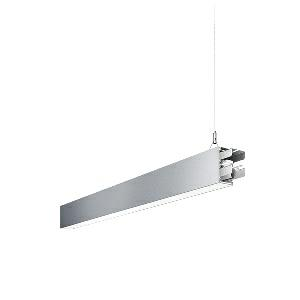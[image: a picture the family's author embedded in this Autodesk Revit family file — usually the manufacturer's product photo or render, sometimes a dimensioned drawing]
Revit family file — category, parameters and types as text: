
# Revit family: dotoo_line_-_dlp_1500_830_d_mid_00805845_2402
name_source: partatom
category: Lighting Fixtures
units: mm (PartAtom-declared; Revit-internal decimal feet)

## family parameters
Cut with Voids When Loaded = No
Host = Face
Light Source = No
Part Type = Normal
Room Calculation Point = No
Round Connector Dimension = Use Diameter
Shared = No

## types (1)
- DOTOO.line - DLP 1500/830/D MID (1 x LED, 1300 lm, 3000K)
    Apparent Load = 13 VA
    Approval mark = CE
    CIE Flux Codes = 67 91 98 100 100
    Color Rendering = 80-89
    Color Temperature = 3000K
    Control Gear = Electronic ballast
    Default Elevation = 1800 mm
    Description = DLP 1500/830/D|Suspended luminaire|light source: LED|connected load: 220-240 V, 50/60 Hz|Power consumption: approx. 13 W|standby: approx. 0,20|luminous flux: 1300 lm|luminous efficacy: 100 lm/W|light distribution: Direct|direct ratio: approx. 100 %|colour temperature: Warm white, ca. 3000 K|color rendering index (CRI): >= 80|chromaticity tolerance:  3 SDCM|System of protection: IP 40|technology: Continuously dimmable|luminaire body|material: Sectional aluminium|colour: Silver|lamp cover: Acrylic (PMMA), Clear|mains lead: 1,0 m With free stranded wires|Fastening: Steel cable 0.3 - 0.7 m|glare control: Prism aperture|luminance(L65): <= 3000 cd/m|unified glare rating(4H 8H): <=  19|special features: DALI Load 1x, TouchDIM - dimming via standard switch, Through-wired, up to 18 m on one mains connection, Flicker-free, Suitable as emergency lighting, Mechanical and electrical connection of the individual modules without tools|
    Frequency = 50 Hz
    Height = 110 mm
    Lamp = 1 x LED
    Lamp Light Flux = 1300 lm
    Lamp count = 1
    Length = 1122 mm
    Luminous efficacy = 100 lm/W
    Manufacturer = Waldmann
    ModVariant = No
    Model = 00805845
    Mounting Place = Ceiling
    Mounting Type = Pendant
    Number of Poles = 1
    OnlyDefault = Yes
    Power Factor = 1
    Product Name = DOTOO.line - DLP 1500/830/D MID
    Product group = Suspended luminaire
    ProductGroupID = 9
    Protection Class = Protection class I
    Protection Degree = IP 40
    RLX_Detail_Level = 1
    RLX_Emergency_Light_Flux = 0 lm
    RLX_Emergency_Type = 0
    RLX_Emergency_Type_DB = No
    RlxData = <blob elided: 21081 chars, md5=0d71e679>
    Socket = socket
    Standby Power = 0 W
    System Light Flux = 1300 lm
    System Power = 13 W
    Type Comments = Product without accessories
    Type Image = 113305000-00692579.jpg
    URL = http://relux.com
    VarID = ---
    Voltage = 230 V
    Voltage Range = 220-240 V
    Weight = 0.00 kg
    Width = 60 mm  [stored 0.19685 ft]

note: [stored X ft] marks values corroborated as IEEE doubles in the binary element streams (Revit-internal decimal feet)

## geometry (parser evidence)
native form markers: Blend x4, Sweep x12
no freeform markers — native parametric forms only
